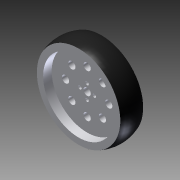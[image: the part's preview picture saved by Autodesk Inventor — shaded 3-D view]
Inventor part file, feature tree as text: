
AUTODESK INVENTOR PART (.ipt)
format: ipt  version: 2013 (Build 170138000, 138)  size: 148,480 bytes
history: native  units: in
note: dims shown in document units (in); Inventor stores cm internally (conversion verified against a paired STEP export)
features: other x1, imported_body x1, plane x1
ambient origin geometry x8: Origin, YZ Plane, XZ Plane, XY Plane, X Axis, Y Axis, Z Axis, Center Point
feature tree (3):
  other  "WHEEL_101MM_4-IN_2011"
  imported_body  "Base1"
  plane  "Work Plane1"
